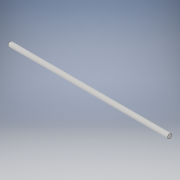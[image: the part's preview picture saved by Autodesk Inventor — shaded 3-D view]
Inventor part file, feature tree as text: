
AUTODESK INVENTOR PART (.ipt)
format: ipt  version: 2019 (Build 230136000, 136)  size: 90,624 bytes
history: native  units: mm
features: extrude x1, sketch x1
ambient origin geometry x8: Origin, YZ Plane, XZ Plane, XY Plane, X Axis, Y Axis, Z Axis, Center Point
bodies: Solid1 (feature_tree)
feature tree (2):
  extrude  "Extrusion1"  Depth=250.0mm TaperAngle=0.0deg
  sketch  "Sketch1"  dims[d0=7.0mm d1=250.0mm d2=0.0mm]
